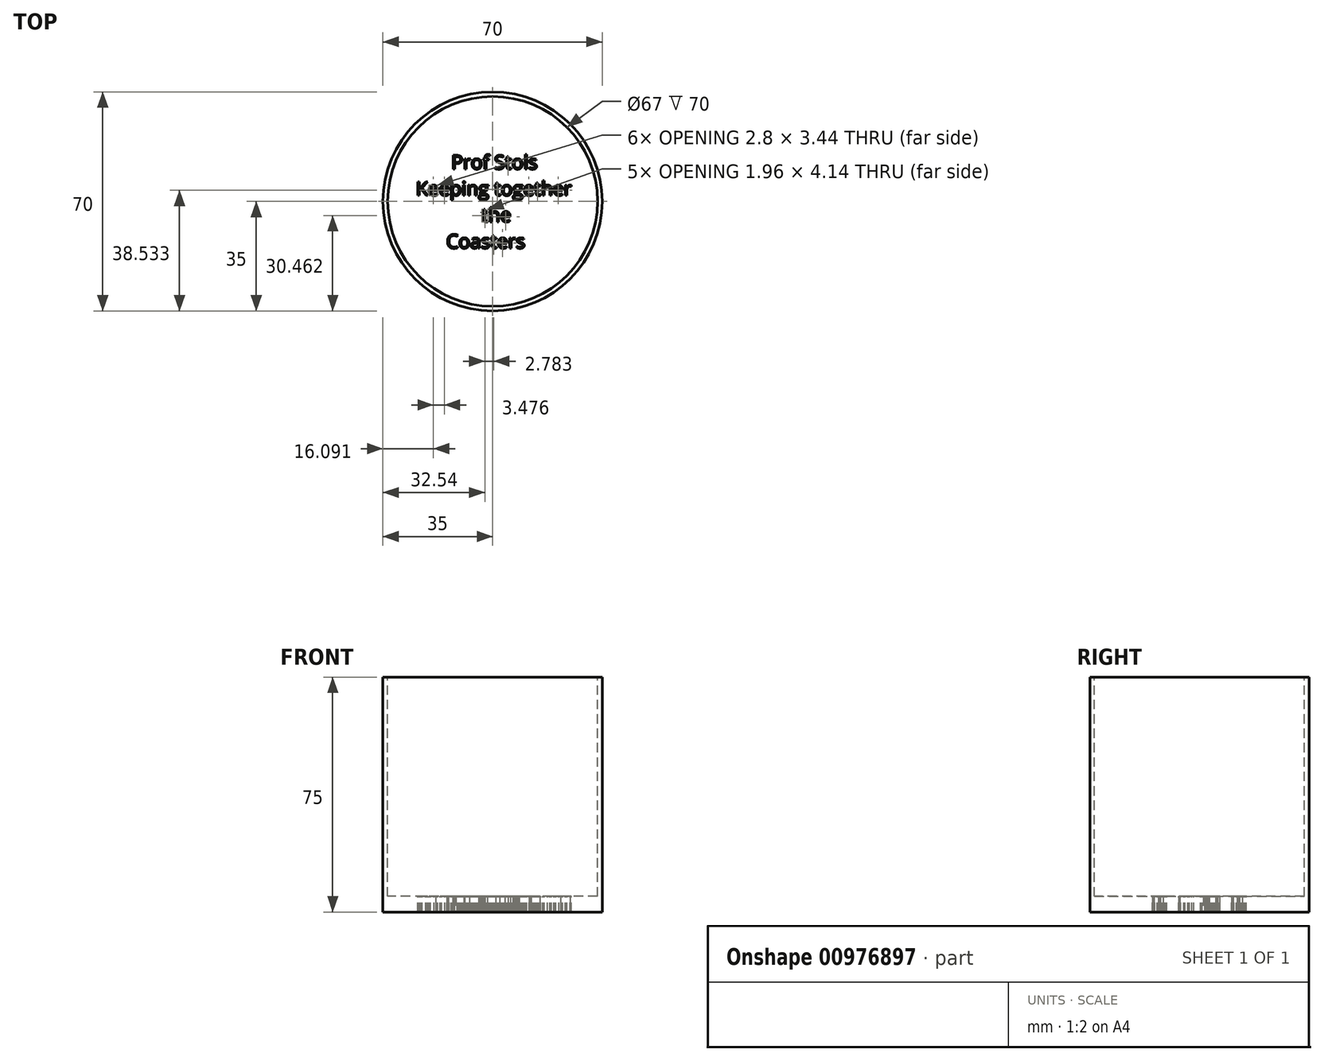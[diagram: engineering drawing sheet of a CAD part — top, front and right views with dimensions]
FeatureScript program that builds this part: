
annotation { "Feature Type Name" : "Feature", "Feature Type Description" : "" }
export const myFeature = defineFeature(function(context is Context, id is Id, definition is map)
    precondition{}
    {
        {
            var Q0;
            Q0=qCreatedBy(makeId("Top.planeOp"),FACE);
            var sketch = newSketch(context, id + "F0", { "sketchPlane" : qUnion([Q0])});
            skCircle(sketch, "E0", {"center": v(0, 0) * mm, "radius": 35 * mm});
            skSolve(sketch);
        }
        {
            var Q0;
            Q0 = qSketchRegion(id + "F0", true);
            extrude(context, id + "F1", {"entities" : qUnion([Q0]), "depth" : 75 * mm, "offsetDistance" : 25 * mm});
        }
        {
            var Q0;
            Q0=makeQuery(id+"F1.opExtrude","CAP_FACE",FACE,{"disambiguationData":[OSD([sQuery(id+"F0.wireOp",EDGE,"E0")])],"isStart":false});
            var sketch = newSketch(context, id + "F2", { "sketchPlane" : qUnion([Q0])});
            skCircle(sketch, "E1", {"center": v(0, 0) * mm, "radius": 33.5 * mm});
            skSolve(sketch);
        }
        {
            var Q0;
            Q0 = qSketchRegion(id + "F2", true);
            extrude(context, id + "F3", {"entities" : qUnion([Q0]), "operationType" : NewBodyOperationType.REMOVE, "oppositeDirection" : true, "depth" : 70 * mm, "offsetDistance" : 25 * mm});
        }
        {
            var Q0;
            Q0=makeQuery(id+"F3.boolean.opBoolean","COPY",FACE,{"derivedFrom":makeQuery(id+"F3.opExtrude","CAP_FACE",FACE,{"disambiguationData":[OSD([sQuery(id+"F2.wireOp",EDGE,"E1")])],"isStart":false})});
            var sketch = newSketch(context, id + "F4", { "sketchPlane" : qUnion([Q0])});
            skText(sketch, "E2", { "text": "       Prof Stols\nKeeping together\n             the \n      Coasters", "fontName": "OpenSans-Regular.ttf"});
            const initialGuessF4  = {"E2": [-0.02446, 0.0103, 1, 0, 0.00446]};
            skSetInitialGuess(sketch, initialGuessF4);
            skSolve(sketch);
        }
        {
            var Q0;
            Q0 = qSketchRegion(id + "F4", true);
            extrude(context, id + "F5", {"entities" : qUnion([Q0]), "operationType" : NewBodyOperationType.REMOVE, "endBound" : BoundingType.THROUGH_ALL, "oppositeDirection" : true, "depth" : 25 * mm, "offsetDistance" : 25 * mm});
        }
    });
